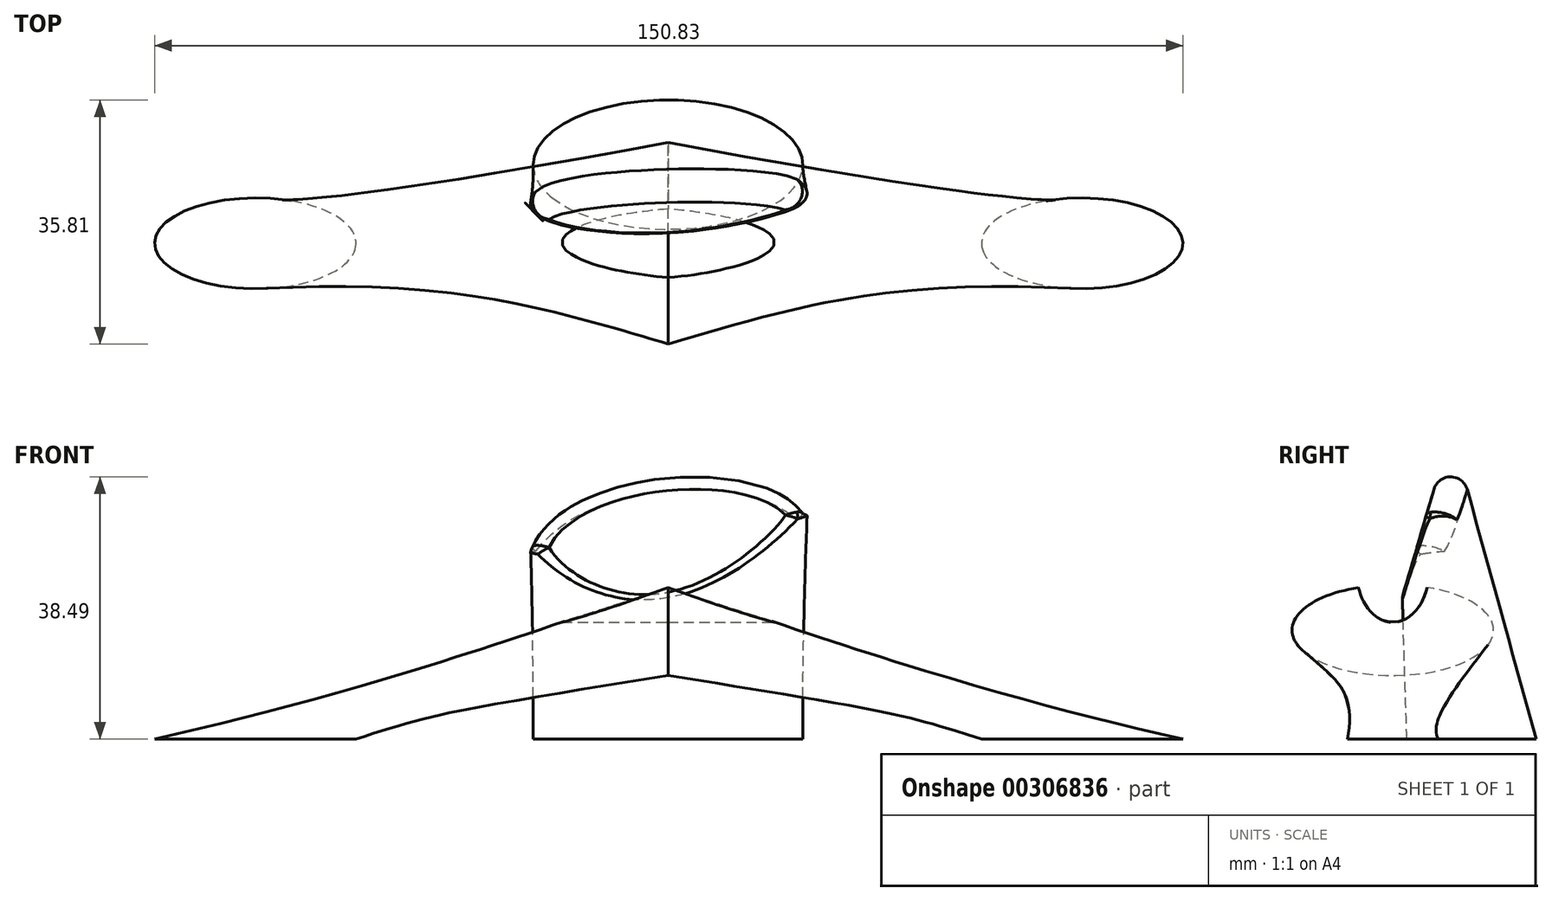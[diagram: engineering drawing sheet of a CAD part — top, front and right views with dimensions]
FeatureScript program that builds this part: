
annotation { "Feature Type Name" : "Feature", "Feature Type Description" : "" }
export const myFeature = defineFeature(function(context is Context, id is Id, definition is map)
    precondition{}
    {
        {
            var Q0;
            Q0=qCreatedBy(makeId("Top.planeOp"),FACE);
            var sketch = newSketch(context, id + "F0", { "sketchPlane" : qUnion([Q0])});
            skEllipse(sketch, "E0", {"center": v(-60.53, 0) * mm, "majorRadius": 14.78 * mm, "minorRadius": 6.66 * mm, "majorAxis": v(-1, 0)});
            skEllipse(sketch, "E1", {"center": v(60.75, 0) * mm, "majorRadius": 14.78 * mm, "minorRadius": 6.66 * mm, "majorAxis": v(-1, 0)});
            skSolve(sketch);
        }
        {
            var Q0;
            Q0=qCreatedBy(makeId("Right.planeOp"),FACE);
            var sketch = newSketch(context, id + "F1", { "sketchPlane" : qUnion([Q0])});
            skEllipse(sketch, "E2", {"center": v(0, 16) * mm, "majorRadius": 14.78 * mm, "minorRadius": 6.66 * mm, "majorAxis": v(-1, 0)});
            skSolve(sketch);
        }
        {
            var Q0;
            Q0=makeQuery(id+"F1.imprint","IMPRINT",FACE,{"disambiguationData":[TD([[makeQuery(id+"F1.imprint","IMPRINT",EDGE,{"derivedFrom":sQuery(id+"F1.wireOp",EDGE,"E2")}),1.0]])]});
            var Q1;
            Q1=makeQuery(id+"F0.imprint","IMPRINT",FACE,{"disambiguationData":[TD([[makeQuery(id+"F0.imprint","IMPRINT",EDGE,{"derivedFrom":sQuery(id+"F0.wireOp",EDGE,"E0")}),1.0]])]});
            loft(context, id + "F2", {"sheetProfilesArray" : [{ "sheetProfileEntities" : qUnion([Q0]) }, { "sheetProfileEntities" : qUnion([Q1]) }]});
        }
        {
            var Q0;
            Q0=makeQuery(id+"F1.imprint","IMPRINT",FACE,{"disambiguationData":[TD([[makeQuery(id+"F1.imprint","IMPRINT",EDGE,{"derivedFrom":sQuery(id+"F1.wireOp",EDGE,"E2")}),1.0]])]});
            var Q1;
            Q1=makeQuery(id+"F0.imprint","IMPRINT",FACE,{"disambiguationData":[TD([[makeQuery(id+"F0.imprint","IMPRINT",EDGE,{"derivedFrom":sQuery(id+"F0.wireOp",EDGE,"E1")}),1.0]])]});
            loft(context, id + "F3", {"sheetProfilesArray" : [{ "sheetProfileEntities" : qUnion([Q0]) }, { "sheetProfileEntities" : qUnion([Q1]) }]});
        }
        {
            var Q0;
            Q0=qCreatedBy(makeId("Right.planeOp"),FACE);
            var sketch = newSketch(context, id + "F4", { "sketchPlane" : qUnion([Q0])});
            skEllipse(sketch, "E3", {"center": v(0, 24.56) * mm, "majorRadius": 7.42 * mm, "minorRadius": 5.3 * mm, "majorAxis": v(0, -1)});
            skSolve(sketch);
        }
        {
            var Q0;
            Q0=makeQuery(id+"F4.imprint","IMPRINT",FACE,{"disambiguationData":[TD([[makeQuery(id+"F4.imprint","IMPRINT",EDGE,{"derivedFrom":sQuery(id+"F4.wireOp",EDGE,"E3")}),1.0]])]});
            extrude(context, id + "F5", {"entities" : qUnion([Q0]), "operationType" : NewBodyOperationType.REMOVE, "endBound" : BoundingType.SYMMETRIC, "oppositeDirection" : true, "depth" : 127 * mm});
        }
        {
            var Q0;
            Q0=qCreatedBy(makeId("Top.planeOp"),FACE);
            var sketch = newSketch(context, id + "F6", { "sketchPlane" : qUnion([Q0])});
            skEllipse(sketch, "E4", {"center": v(0, 11.54) * mm, "majorRadius": 19.77 * mm, "minorRadius": 9.48 * mm, "majorAxis": v(-1, 0)});
            skSolve(sketch);
        }
        {
            var Q0;
            Q0=qCreatedBy(makeId("Front.planeOp"),FACE);
            var sketch = newSketch(context, id + "F7", { "sketchPlane" : qUnion([Q0])});
            skEllipse(sketch, "E5", {"center": v(0, 70.26) * mm, "majorRadius": 22.62 * mm, "minorRadius": 6.8 * mm, "majorAxis": v(-1, 0)});
            skSolve(sketch);
        }
        {
            var Q0;
            Q0=makeQuery(id+"F7.imprint","IMPRINT",FACE,{"disambiguationData":[TD([[makeQuery(id+"F7.imprint","IMPRINT",EDGE,{"derivedFrom":sQuery(id+"F7.wireOp",EDGE,"E5")}),1.0]])]});
            var Q1;
            Q1=makeQuery(id+"F6.imprint","IMPRINT",FACE,{"disambiguationData":[TD([[makeQuery(id+"F6.imprint","IMPRINT",EDGE,{"derivedFrom":sQuery(id+"F6.wireOp",EDGE,"E4")}),1.0]])]});
            loft(context, id + "F8", {"sheetProfilesArray" : [{ "sheetProfileEntities" : qUnion([Q0]) }, { "sheetProfileEntities" : qUnion([Q1]) }]});
        }
        {
            var Q0;
            Q0=qCreatedBy(makeId("Right.planeOp"),FACE);
            var sketch = newSketch(context, id + "F9", { "sketchPlane" : qUnion([Q0])});
            skLineSegment(sketch, "E6", {"start": v(1.2, 20.15) * mm, "end": v(9.99, 50.11) * mm});
            skLineSegment(sketch, "E7", {"start": v(9.99, 50.11) * mm, "end": v(0, 81.87) * mm});
            skLineSegment(sketch, "E8", {"start": v(0, 81.87) * mm, "end": v(-8.93, 71.23) * mm});
            skLineSegment(sketch, "E9", {"start": v(-8.93, 71.23) * mm, "end": v(1.2, 20.15) * mm});
            skSolve(sketch);
        }
        {
            var Q0;
            Q0=makeQuery(id+"F9.imprint","IMPRINT",FACE,{"disambiguationData":[TD([[makeQuery(id+"F9.imprint","IMPRINT",EDGE,{"derivedFrom":sQuery(id+"F9.wireOp",EDGE,"E6")}),1.0]])]});
            extrude(context, id + "F10", {"entities" : qUnion([Q0]), "operationType" : NewBodyOperationType.REMOVE, "endBound" : BoundingType.SYMMETRIC, "oppositeDirection" : true, "depth" : 76.2 * mm});
        }
        {
            var Q0;
            Q0=makeQuery(id+"F10.boolean.opBoolean","INTERSECT",EDGE,{"derivedFrom":[makeQuery(id+"F8.opLoft","SWEPT_FACE",FACE,{"disambiguationData":[OSD([sQuery(id+"F6.wireOp",EDGE,"E4"),sQuery(id+"F7.wireOp",EDGE,"E5")])]}),makeQuery(id+"F10.opExtrude","SWEPT_FACE",FACE,{"disambiguationData":[OSD([sQuery(id+"F9.wireOp",EDGE,"E6")])]})]});
            fillet(context, id + "F11", {"entities" : qUnion([Q0]), "radius" : 2.54 * mm, "tangentPropagation" : true, "allowEdgeOverflow" : false});
        }
    });
